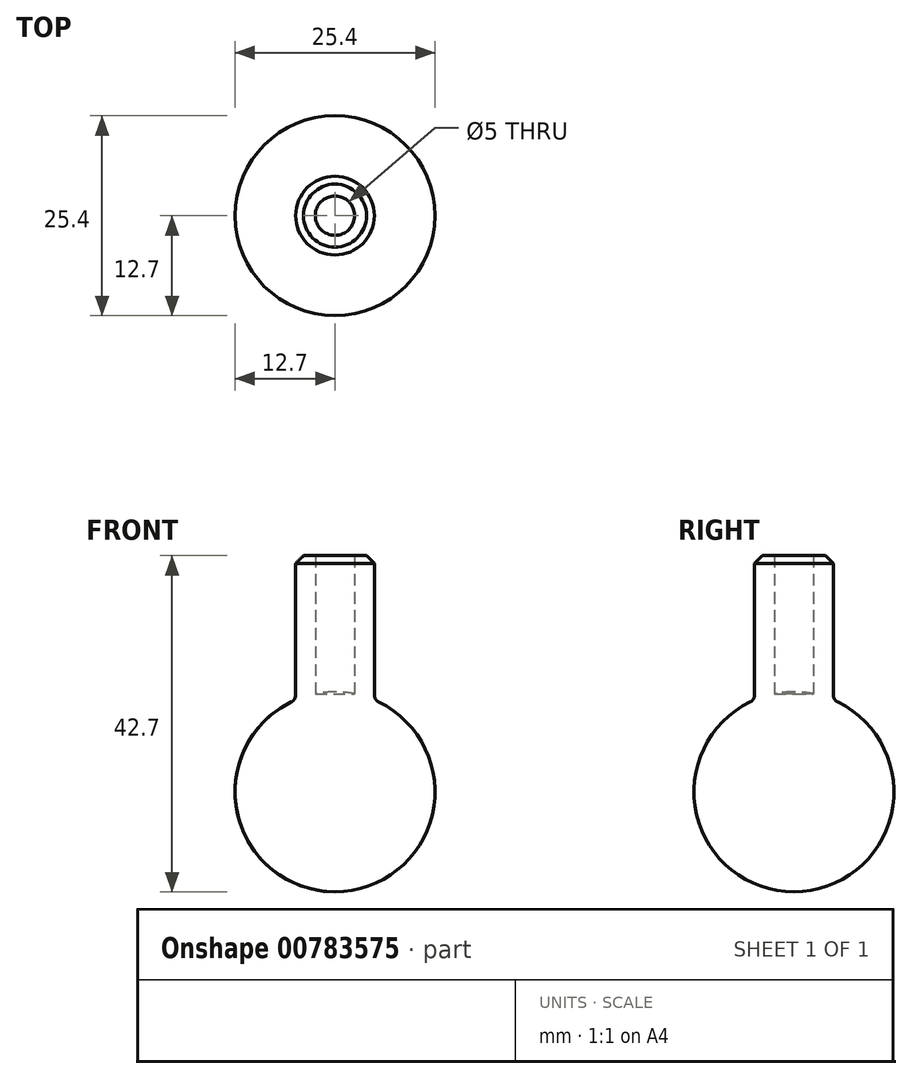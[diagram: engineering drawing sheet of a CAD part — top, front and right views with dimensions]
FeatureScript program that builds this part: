
annotation { "Feature Type Name" : "Feature", "Feature Type Description" : "" }
export const myFeature = defineFeature(function(context is Context, id is Id, definition is map)
    precondition{}
    {
        {
            var Q0;
            Q0=qCreatedBy(makeId("Front.planeOp"),FACE);
            var sketch = newSketch(context, id + "F0", { "sketchPlane" : qUnion([Q0])});
            skLineSegment(sketch, "E0", {"start": v(0, 0) * mm, "end": v(0, 30.82) * mm, "construction": true});
            skArc(sketch, "E1", {"start": v(0, -12.7) * mm, "mid": v(12.7, 0) * mm, "end": v(0, 12.7) * mm});
            skLineSegment(sketch, "E2", {"start": v(0, 12.7) * mm, "end": v(0, -12.7) * mm});
            skSolve(sketch);
        }
        {
            var Q0;
            Q0 = qSketchRegion(id + "F0", true);
            var Q1;
            Q1=sQuery(id+"F0.wireOp",EDGE,"E0");
            revolve(context, id + "F1", {"surfaceOperationType" : NewSurfaceOperationType.NEW, "entities" : qUnion([Q0]), "axis" : qUnion([Q1]), "revolveType" : RevolveType.FULL});
        }
        {
            var Q0;
            Q0=qCreatedBy(makeId("Front.planeOp"),FACE);
            var sketch = newSketch(context, id + "F2", { "sketchPlane" : qUnion([Q0])});
            skLineSegment(sketch, "E3", {"start": v(0, 0) * mm, "end": v(0, 44.86) * mm, "construction": true});
            skLineSegment(sketch, "E4.bottom", {"start": v(-2.5, 30) * mm, "end": v(-5, 30) * mm});
            skLineSegment(sketch, "E4.top", {"start": v(-2.5, 0) * mm, "end": v(-5, 0) * mm});
            skLineSegment(sketch, "E4.left", {"start": v(-2.5, 30) * mm, "end": v(-2.5, 0) * mm});
            skLineSegment(sketch, "E4.right", {"start": v(-5, 30) * mm, "end": v(-5, 0) * mm});
            skSolve(sketch);
        }
        {
            var Q0;
            Q0 = qSketchRegion(id + "F2", true);
            var Q1;
            Q1=sQuery(id+"F2.wireOp",EDGE,"E3");
            revolve(context, id + "F3", {"operationType" : NewBodyOperationType.ADD, "surfaceOperationType" : NewSurfaceOperationType.NEW, "entities" : qUnion([Q0]), "axis" : qUnion([Q1]), "revolveType" : RevolveType.FULL});
        }
        {
            var Q0;
            Q0=makeQuery(id+"F3.opRevolve","SWEPT_EDGE",EDGE,{"disambiguationData":[OSD([sQuery(id+"F2.wireOp",EDGE,"E4.bottom"),sQuery(id+"F2.wireOp",EDGE,"E4.right")])]});
            chamfer(context, id + "F4", {"entities" : qUnion([Q0]), "width" : 1 * mm, "tangentPropagation" : true});
        }
        {
            var Q0;
            Q0=makeQuery(id+"F3.boolean.opBoolean","INTERSECT",EDGE,{"derivedFrom":[makeQuery(id+"F1.opRevolve","SWEPT_FACE",FACE,{"disambiguationData":[OSD([sQuery(id+"F0.wireOp",EDGE,"E1")])]}),makeQuery(id+"F3.opRevolve","SWEPT_FACE",FACE,{"disambiguationData":[OSD([sQuery(id+"F2.wireOp",EDGE,"E4.right")])]})]});
            fillet(context, id + "F5", {"entities" : qUnion([Q0]), "radius" : 1 * mm, "tangentPropagation" : true, "allowEdgeOverflow" : false});
        }
    });
